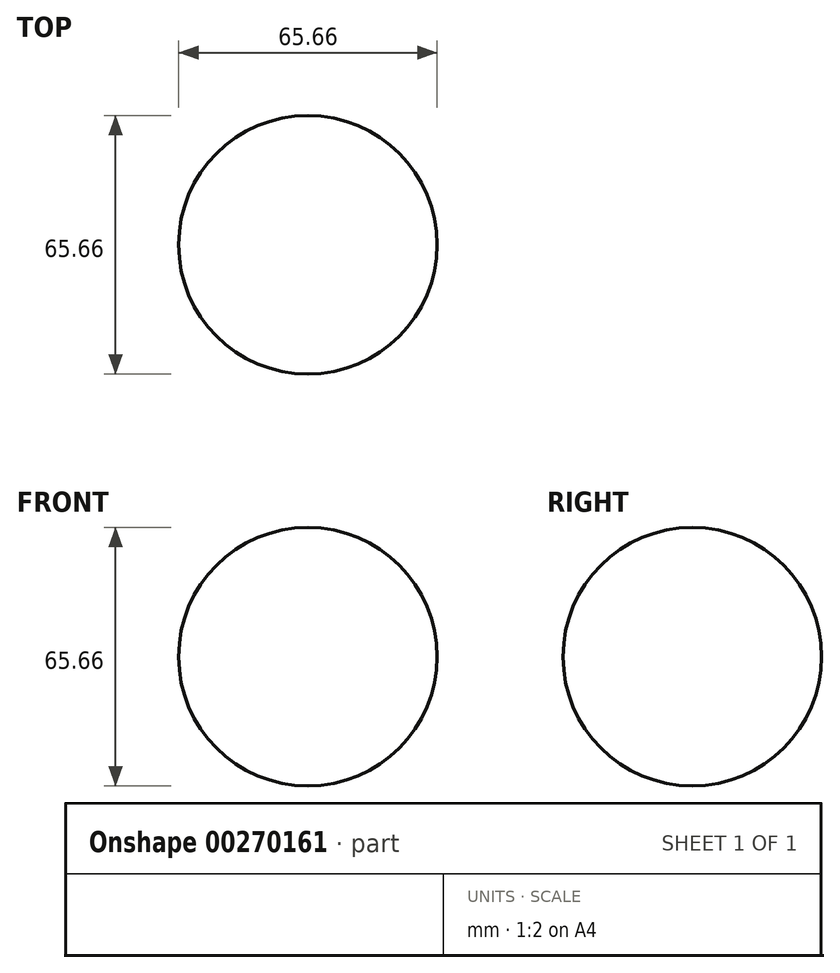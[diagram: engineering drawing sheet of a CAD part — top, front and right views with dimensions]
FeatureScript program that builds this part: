
annotation { "Feature Type Name" : "Feature", "Feature Type Description" : "" }
export const myFeature = defineFeature(function(context is Context, id is Id, definition is map)
    precondition{}
    {
        {
            var Q0;
            Q0=qCreatedBy(makeId("Front.planeOp"),FACE);
            var sketch = newSketch(context, id + "F0", { "sketchPlane" : qUnion([Q0])});
            skArc(sketch, "E0", {"start": v(0, 32.83) * mm, "mid": v(-32.83, 0) * mm, "end": v(0, -32.83) * mm});
            skLineSegment(sketch, "E1", {"start": v(0, 32.83) * mm, "end": v(0, -32.83) * mm});
            skSolve(sketch);
        }
        {
            var Q0;
            Q0=qCreatedBy(makeId("Front.planeOp"),FACE);
            var sketch = newSketch(context, id + "F1", { "sketchPlane" : qUnion([Q0])});
            skLineSegment(sketch, "E2", {"start": v(0, 37.59) * mm, "end": v(0, -51.21) * mm});
            skSolve(sketch);
        }
        {
            var Q0;
            Q0=makeQuery(id+"F0.imprint","IMPRINT",FACE,{"disambiguationData":[TD([[makeQuery(id+"F0.imprint","IMPRINT",EDGE,{"derivedFrom":sQuery(id+"F0.wireOp",EDGE,"E0")}),1.0]])]});
            var Q1;
            Q1=sQuery(id+"F1.wireOp",EDGE,"E2");
            revolve(context, id + "F2", {"entities" : qUnion([Q0]), "axis" : qUnion([Q1]), "revolveType" : RevolveType.FULL});
        }
    });
